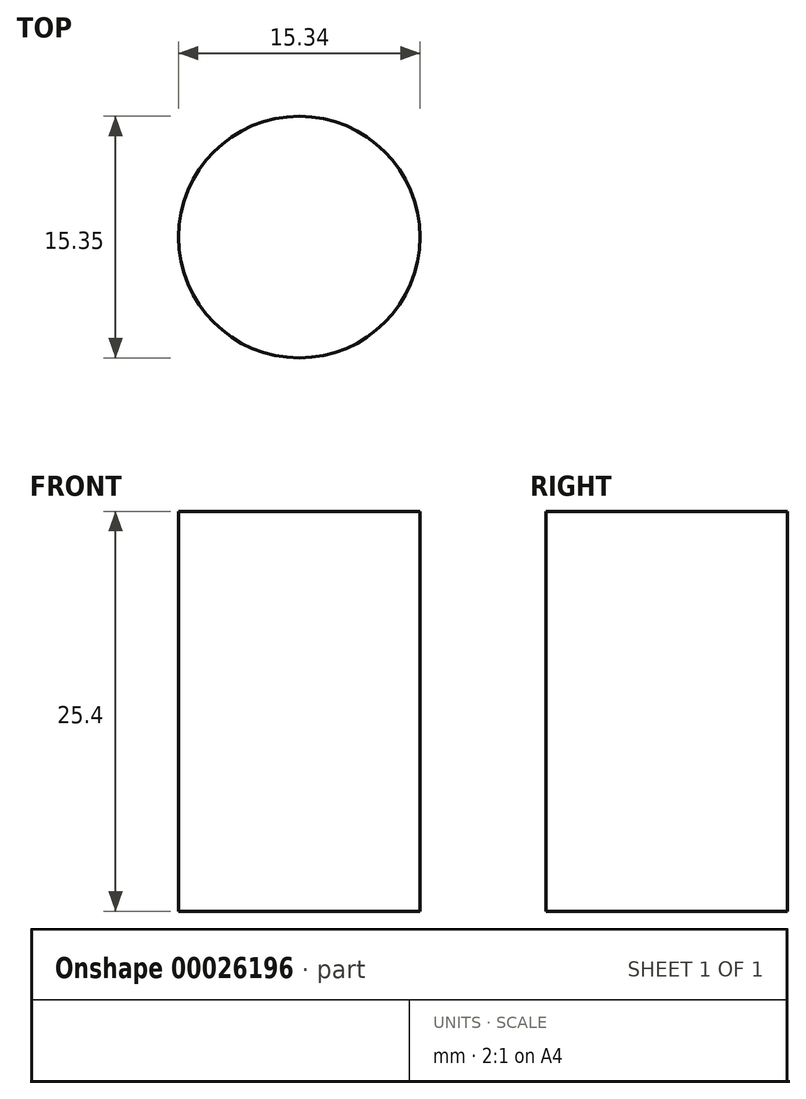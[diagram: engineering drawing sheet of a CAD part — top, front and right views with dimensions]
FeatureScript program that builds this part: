
annotation { "Feature Type Name" : "Feature", "Feature Type Description" : "" }
export const myFeature = defineFeature(function(context is Context, id is Id, definition is map)
    precondition{}
    {
        {
            var Q0;
            Q0=qCreatedBy(makeId("Top.planeOp"),FACE);
            var sketch = newSketch(context, id + "F0", { "sketchPlane" : qUnion([Q0])});
            skLineSegment(sketch, "E0.rect.bottom", {"start": v(-87.17, -31.79) * mm, "end": v(-140.37, -31.79) * mm});
            skLineSegment(sketch, "E0.rect.top", {"start": v(-87.17, 8.97) * mm, "end": v(-140.37, 8.97) * mm});
            skLineSegment(sketch, "E0.rect.left", {"start": v(-87.17, -31.79) * mm, "end": v(-87.17, 8.97) * mm});
            skLineSegment(sketch, "E0.rect.right", {"start": v(-140.37, -31.79) * mm, "end": v(-140.37, 8.97) * mm});
            skPoint(sketch, "E0.rect.middle", {"position": v(-113.77, -11.4) * mm});
            skCircle(sketch, "E1", {"center": v(-87.17, -11.4) * mm, "radius": 20.38 * mm});
            skSolve(sketch);
        }
        {
            var Q0;
            Q0=qCreatedBy(makeId("Top.planeOp"),FACE);
            var sketch = newSketch(context, id + "F1", { "sketchPlane" : qUnion([Q0])});
            skCircle(sketch, "E2", {"center": v(-87.26, -10.96) * mm, "radius": 7.67 * mm});
            skSolve(sketch);
        }
        {
            var Q0;
            Q0 = qSketchRegion(id + "F1", true);
            extrude(context, id + "F2", {"entities" : qUnion([Q0]), "depth" : 25.4 * mm});
        }
    });
